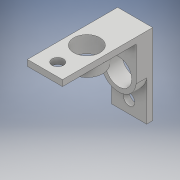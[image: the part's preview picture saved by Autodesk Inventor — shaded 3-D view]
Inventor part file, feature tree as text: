
AUTODESK INVENTOR PART (.ipt)
format: ipt  version: 2017 (Build 210142000, 142)  size: 196,096 bytes
history: native  units: mm
features: extrude x4, sketch x4, projected_geometry x3, chamfer x1
ambient origin geometry x8: Origin, YZ Plane, XZ Plane, XY Plane, X Axis, Y Axis, Z Axis, Center Point
bodies: Solid1 (feature_tree)
feature tree (12):
  extrude  "Extrusion1"  Depth=2.0mm
  extrude  "Extrusion5"  Depth=4.0mm
  extrude  "Extrusion6"  Depth=30.0mm
  chamfer  "Chamfer1"  Distance=2.0mm
  extrude  "Extrusion7"  Depth=3.5mm TaperAngle=45.0deg
  sketch  "Sketch1"  dims[d8=2.0mm d9=0.0mm d27=3.8mm d28=4.0mm d29=0.016443mm]
  sketch  "Sketch5"  dims[d31=2.5mm d36=4.0mm]
  projected_geometry  "Projected Loop2"
  sketch  "Sketch6"  dims[d38=3.8mm d40=0.016443mm d41=2.5mm d42=4.0mm d43=30.0mm d44=2.0mm d45=0.0mm]
  projected_geometry  "Projected Loop3"
  sketch  "Sketch8"  dims[d46=3.5mm d47=0.0mm d48=0.5mm d49=3.5mm d50=45.0deg d51=3.5mm d52=0.0mm d53=5.5mm d54=5.5mm]
  projected_geometry  "Projected Loop5"
